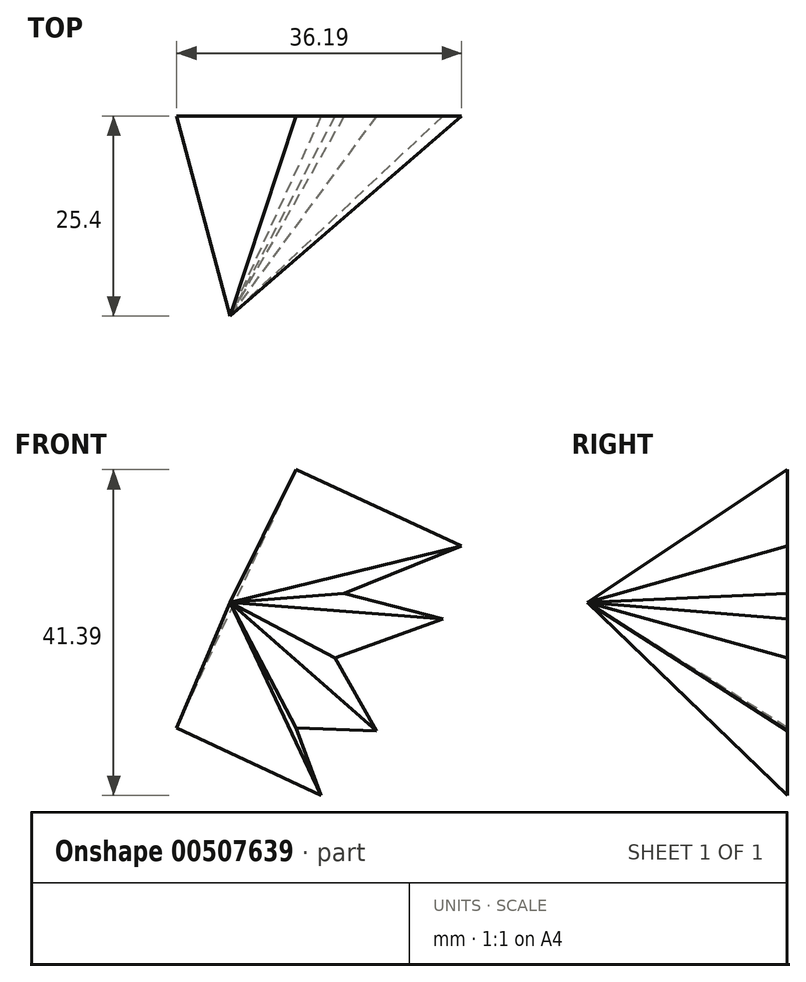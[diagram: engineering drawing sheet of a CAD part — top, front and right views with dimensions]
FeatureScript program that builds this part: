
annotation { "Feature Type Name" : "Feature", "Feature Type Description" : "" }
export const myFeature = defineFeature(function(context is Context, id is Id, definition is map)
    precondition{}
    {
        {
            var Q0;
            Q0=qCreatedBy(makeId("Front.planeOp"),FACE);
            var sketch = newSketch(context, id + "F0", { "sketchPlane" : qUnion([Q0])});
            skLineSegment(sketch, "E0", {"start": v(-41.39, 0) * mm, "end": v(-26.23, 32.8) * mm});
            skLineSegment(sketch, "E1", {"start": v(-26.23, 32.8) * mm, "end": v(-5.2, 23.07) * mm});
            skLineSegment(sketch, "E2", {"start": v(-5.2, 23.07) * mm, "end": v(-20.11, 17.05) * mm});
            skLineSegment(sketch, "E3", {"start": v(-20.11, 17.05) * mm, "end": v(-7.58, 13.85) * mm});
            skLineSegment(sketch, "E4", {"start": v(-7.58, 13.85) * mm, "end": v(-21.28, 8.9) * mm});
            skLineSegment(sketch, "E5", {"start": v(-21.28, 8.9) * mm, "end": v(-16.03, -0.44) * mm});
            skLineSegment(sketch, "E6", {"start": v(-16.03, -0.44) * mm, "end": v(-26.23, 0) * mm});
            skLineSegment(sketch, "E7", {"start": v(-26.23, 0) * mm, "end": v(-23.03, -8.6) * mm});
            skLineSegment(sketch, "E8", {"start": v(-41.39, 0) * mm, "end": v(-23.03, -8.6) * mm});
            skSolve(sketch);
        }
        {
            var Q0;
            Q0=qCreatedBy(makeId("Front.planeOp"),FACE);
            cPlane(context, id + "F1", {"entities" : qUnion([Q0]), "cplaneType" : CPlaneType.OFFSET, "offset" : 25.4 * mm, "width" : 152.4 * mm, "height" : 152.4 * mm});
        }
        {
            var Q0;
            Q0=qCreatedBy(id+"F1.planeOp",FACE);
            var sketch = newSketch(context, id + "F2", { "sketchPlane" : qUnion([Q0])});
            skPoint(sketch, "E9", {"position": v(-34.64, 15.92) * mm});
            skSolve(sketch);
        }
        {
            var Q0;
            Q0=makeQuery(id+"F0.imprint","IMPRINT",FACE,{"disambiguationData":[TD([[makeQuery(id+"F0.imprint","IMPRINT",EDGE,{"derivedFrom":sQuery(id+"F0.wireOp",EDGE,"E0")}),-1.0]])]});
            var Q1;
            Q1=sQuery(id+"F2.wireOp",VERTEX,"E9");
            loft(context, id + "F3", {"sheetProfilesArray" : [{ "sheetProfileEntities" : qUnion([Q0]) }, { "sheetProfileEntities" : qUnion([Q1]) }]});
        }
    });
